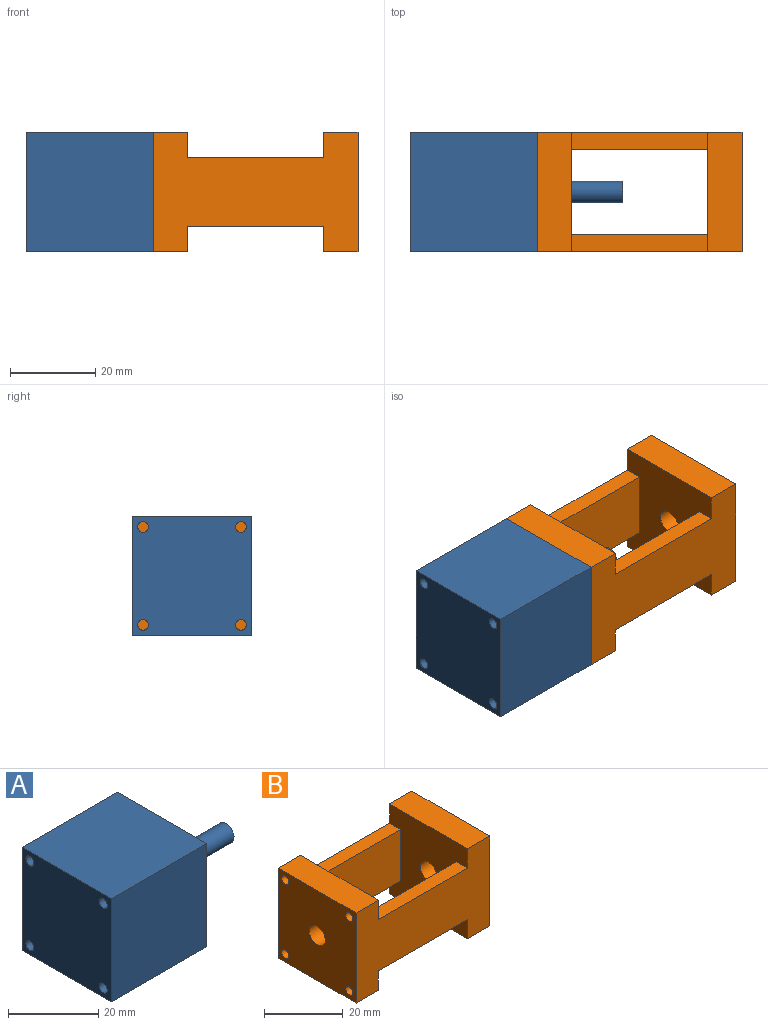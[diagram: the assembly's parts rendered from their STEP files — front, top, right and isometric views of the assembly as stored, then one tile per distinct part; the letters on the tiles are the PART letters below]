
ASSEMBLY  parts=2 mates=1
PART A: 12 faces, bbox 50x28x28 mm
  f0: plane 30x28mm, normal (0,1,0), area 840mm2, adj f1,f6,f8,f9
  f1: plane 30x28mm, normal (0,0,1), area 840mm2, adj f0,f2,f8,f9
  f2: plane 30x28mm, normal (0,-1,0), area 840mm2, adj f1,f6,f8,f9
  f3: cylinder r=1.25mm len=30mm, axis (-1,0,0), area 235.6mm2, adj f8,f9
  f4: cylinder r=1.25mm len=30mm, axis (-1,0,0), area 235.6mm2, adj f8,f9
  f5: cylinder r=1.25mm len=30mm, axis (-1,0,0), area 235.6mm2, adj f8,f9
  f6: plane 30x28mm, normal (0,0,-1), area 840mm2, adj f0,f2,f8,f9
  f7: cylinder r=1.25mm len=30mm, axis (-1,0,0), area 235.6mm2, adj f8,f9
  f8: plane 28x28mm, normal (1,0,0), area 744.7mm2, adj f0,f1,f2,f3,f4,f5,f6,f7
  f9: plane 28x28mm, normal (-1,0,0), area 764.4mm2, adj f0,f1,f2,f3,f4,f5,f6,f7
  f10: cylinder r=2.5mm len=20mm, axis (-1,0,0), area 314.2mm2, adj f8,f11
  f11: plane 5x5mm, normal (1,0,0), area 19.6mm2, adj f10
PART B: 22 faces, bbox 48x28x28 mm
  f0: plane 28x28mm, normal (1,0,0), area 609.9mm2, adj f1,f2,f3,f4,f5,f7,f8,f9
  f1: plane 48x28mm, normal (0,1,0), area 960mm2, adj f0,f2,f4,f6,f14,f16,f17,f18
  f2: plane 28x8mm, normal (0,0,1), area 224mm2, adj f0,f1,f3,f6
  f3: plane 48x28mm, normal (0,-1,0), area 960mm2, adj f0,f2,f4,f6,f11,f12,f17,f18
  f4: plane 28x8mm, normal (0,0,-1), area 224mm2, adj f0,f1,f3,f6
  f5: cylinder r=2.9mm len=8mm, axis (-1,0,0), area 145.8mm2, adj f0,f6
  f6: plane 28x28mm, normal (-1,0,0), area 737.9mm2, adj f1,f2,f3,f4,f5,f7,f8,f9
  f7: cylinder r=1.25mm len=8mm, axis (1,0,0), area 62.8mm2, adj f0,f6
  f8: cylinder r=1.25mm len=8mm, axis (1,0,0), area 62.8mm2, adj f0,f6
  f9: cylinder r=1.25mm len=8mm, axis (1,0,0), area 62.8mm2, adj f0,f6
  f10: cylinder r=1.25mm len=8mm, axis (1,0,0), area 62.8mm2, adj f0,f6
  f11: plane 32x4mm, normal (0,0,1), area 128mm2, adj f0,f3,f13,f17
  f12: plane 32x4mm, normal (0,0,-1), area 128mm2, adj f0,f3,f13,f17
  f13: plane 32x16mm, normal (0,1,0), area 512mm2, adj f0,f11,f12,f17
  f14: plane 32x4mm, normal (0,0,1), area 128mm2, adj f0,f1,f15,f17
  f15: plane 32x16mm, normal (0,-1,0), area 512mm2, adj f0,f14,f16,f17
  f16: plane 32x4mm, normal (0,0,-1), area 128mm2, adj f0,f1,f15,f17
  f17: plane 28x28mm, normal (-1,0,0), area 629.6mm2, adj f1,f3,f11,f12,f13,f14,f15,f16
  f18: plane 28x8mm, normal (0,0,1), area 224mm2, adj f1,f3,f17,f21
  f19: plane 28x8mm, normal (0,0,-1), area 224mm2, adj f1,f3,f17,f21
  f20: cylinder r=2.9mm len=8mm, axis (-1,0,0), area 145.8mm2, adj f17,f21
  f21: plane 28x28mm, normal (1,0,0), area 757.6mm2, adj f1,f3,f18,f19,f20
PLACE A t=(12.18,0.07,0.07)mm
PLACE B t=(42.18,0.07,0.07)mm
MATE planar A.f8 <-> B.f6  axis (1,0,0) through (42.18,-13.93,0.07)mm
